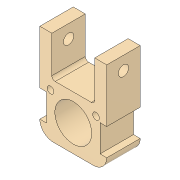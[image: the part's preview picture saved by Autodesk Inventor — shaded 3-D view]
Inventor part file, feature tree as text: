
AUTODESK INVENTOR PART (.ipt)
format: ipt  version: 2018.3 (Build 223284000, 284)  size: 307,712 bytes
history: native  units: in
note: dims shown in document units (in); Inventor stores cm internally (conversion verified against a paired STEP export)
features: extrude x5, sketch x5, fillet x2
ambient origin geometry x8: Origin, YZ Plane, XZ Plane, XY Plane, X Axis, Y Axis, Z Axis, Center Point
bodies: Solid1 (feature_tree)
feature tree (12):
  extrude  "Extrusion1"  Depth=0.625in TaperAngle=0.0deg
  extrude  "Extrusion2"  Depth=0.625in TaperAngle=0.0deg
  extrude  "Extrusion3"  Depth=0.625in TaperAngle=0.0deg
  fillet  "Fillet1"  Radius=0.0625in
  fillet  "Fillet3"  Radius=0.25in
  extrude  "Extrusion4"  Depth=0.8in
  extrude  "Extrusion5"  Depth=1.0in
  sketch  "Sketch1"  dims[d0=1.0in d1=0.225in d2=0.225in d3=0.75in d4=1.25in d8=0.625in d9=0.0in]
  sketch  "Sketch2"  dims[d10=0.6885in d13=0.5in d14=0.625in d15=0.0in]
  sketch  "Sketch3"  dims[d16=0.1925in d17=0.25in d18=0.0in d19=0.625in d20=0.0in d21=0.0625in d23=0.25in]
  sketch  "Sketch4"  dims[d24=0.8in d25=0.126in]
  sketch  "Sketch5"  dims[d26=0.125in d27=0.2in d28=0.125in d29=0.2in d30=1.0in d31=0.0in d32=0.126in d33=0.505in d34=0.125in d35=0.125in d38=1.0in d39=0.0in d41=0.0in]
